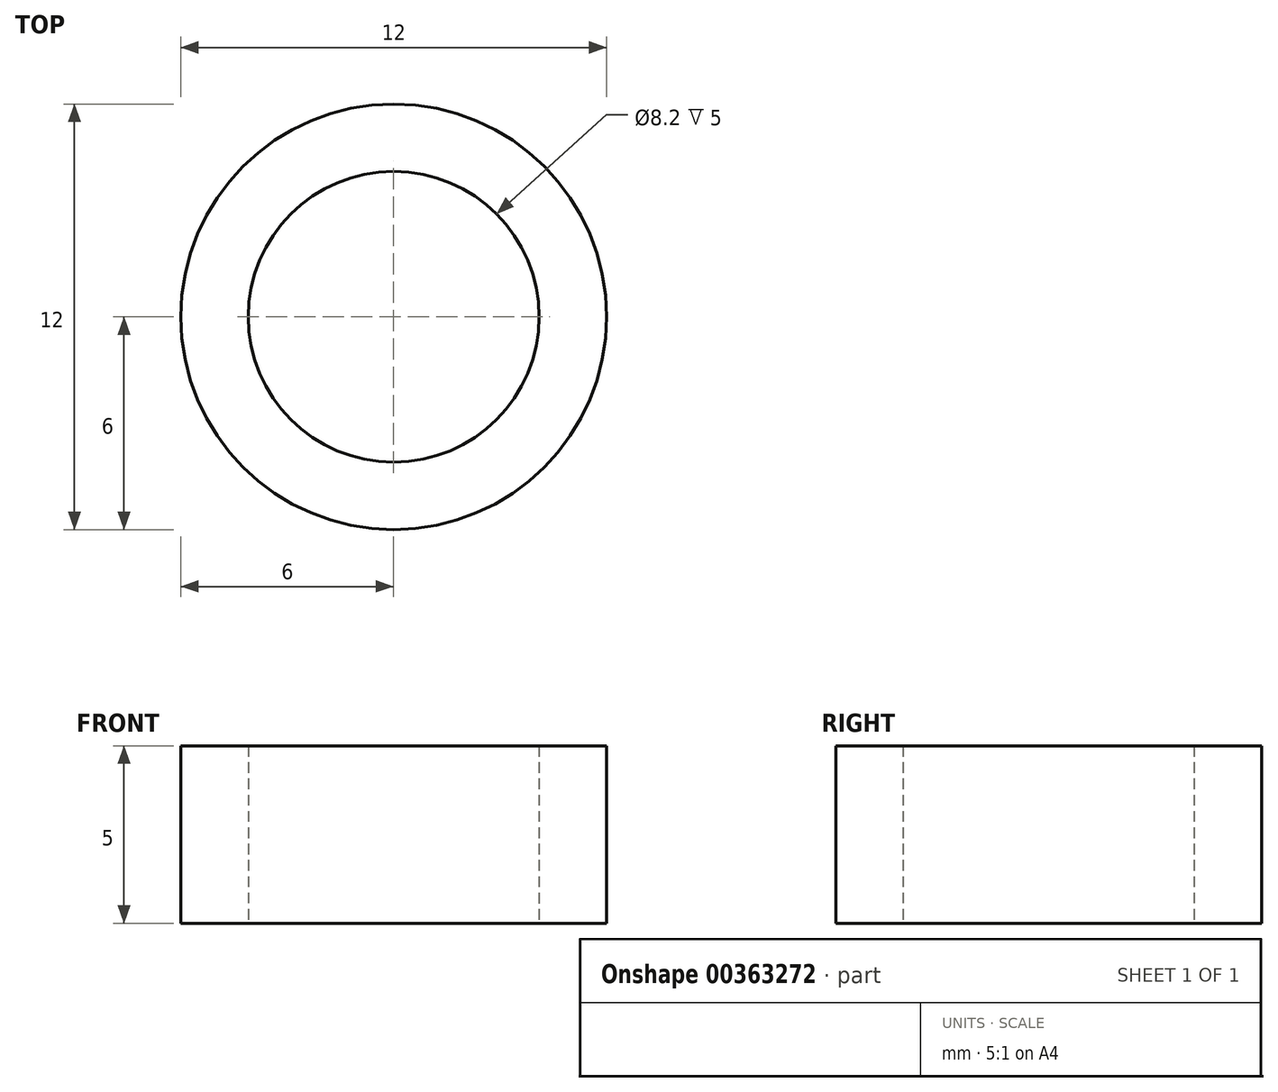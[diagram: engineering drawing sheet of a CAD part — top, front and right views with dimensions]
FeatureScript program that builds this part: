
annotation { "Feature Type Name" : "Feature", "Feature Type Description" : "" }
export const myFeature = defineFeature(function(context is Context, id is Id, definition is map)
    precondition{}
    {
        {
            var Q0;
            Q0=qCreatedBy(makeId("Top.planeOp"),FACE);
            var sketch = newSketch(context, id + "F0", { "sketchPlane" : qUnion([Q0])});
            skCircle(sketch, "E0", {"center": v(0, 0) * mm, "radius": 6 * mm});
            skCircle(sketch, "E1", {"center": v(0, 0) * mm, "radius": 4.1 * mm});
            skSolve(sketch);
        }
        {
            var Q0;
            Q0=makeQuery(id+"F0.imprint","IMPRINT",FACE,{"disambiguationData":[TD([[makeQuery(id+"F0.imprint","IMPRINT",EDGE,{"derivedFrom":sQuery(id+"F0.wireOp",EDGE,"E0")}),1.0]])]});
            extrude(context, id + "F1", {"entities" : qUnion([Q0]), "depth" : 5 * mm});
        }
    });
